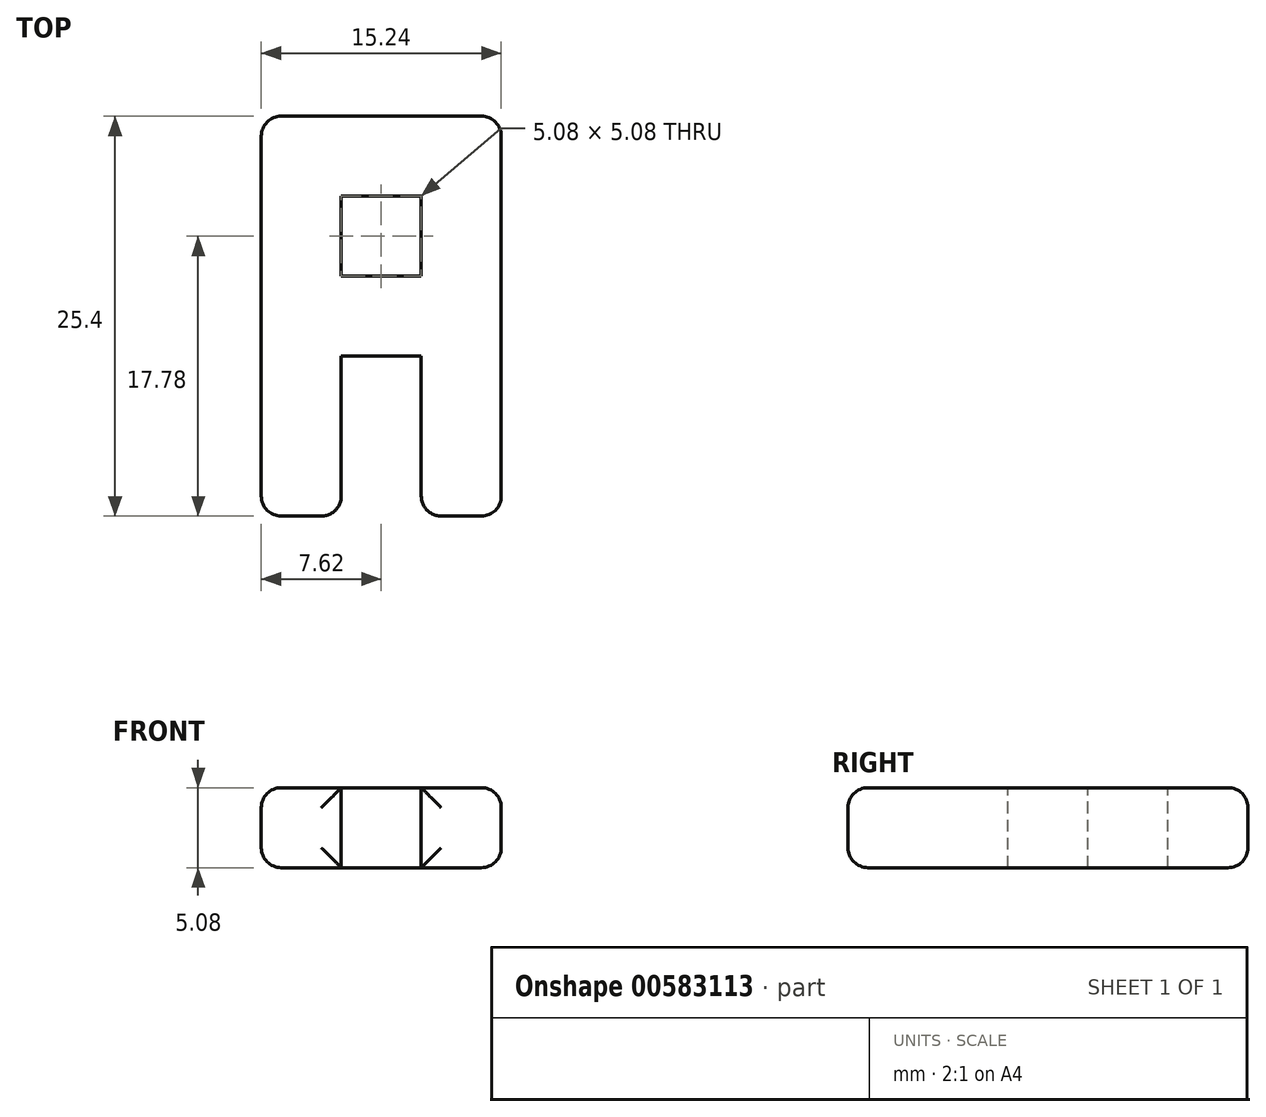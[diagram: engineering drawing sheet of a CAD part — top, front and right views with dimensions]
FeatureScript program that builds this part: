
annotation { "Feature Type Name" : "Feature", "Feature Type Description" : "" }
export const myFeature = defineFeature(function(context is Context, id is Id, definition is map)
    precondition{}
    {
        {
            var Q0;
            Q0=qCreatedBy(makeId("Top.planeOp"),FACE);
            var sketch = newSketch(context, id + "F0", { "sketchPlane" : qUnion([Q0])});
            skLineSegment(sketch, "E0.bottom", {"start": v(7.62, 12.7) * mm, "end": v(-7.62, 12.7) * mm});
            skLineSegment(sketch, "E0.top", {"start": v(7.62, -12.7) * mm, "end": v(-7.62, -12.7) * mm});
            skLineSegment(sketch, "E0.left", {"start": v(7.62, 12.7) * mm, "end": v(7.62, -12.7) * mm});
            skLineSegment(sketch, "E0.right", {"start": v(-7.62, 12.7) * mm, "end": v(-7.62, -12.7) * mm});
            skPoint(sketch, "E0.middle", {"position": v(0, 0) * mm});
            skSolve(sketch);
        }
        {
            var Q0;
            Q0=makeQuery(id+"F0.imprint","IMPRINT",FACE,{"disambiguationData":[TD([[makeQuery(id+"F0.imprint","IMPRINT",EDGE,{"derivedFrom":sQuery(id+"F0.wireOp",EDGE,"E0.bottom")}),1.0]])]});
            extrude(context, id + "F1", {"entities" : qUnion([Q0]), "depth" : 5.08 * mm, "offsetDistance" : 25.4 * mm});
        }
        {
            var Q0;
            Q0=makeQuery(id+"F1.opExtrude","CAP_FACE",FACE,{"disambiguationData":[OSD([sQuery(id+"F0.wireOp",EDGE,"E0.bottom"),sQuery(id+"F0.wireOp",EDGE,"E0.top"),sQuery(id+"F0.wireOp",EDGE,"E0.left"),sQuery(id+"F0.wireOp",EDGE,"E0.right")])],"isStart":false});
            var sketch = newSketch(context, id + "F2", { "sketchPlane" : qUnion([Q0])});
            skLineSegment(sketch, "E1.bottom", {"start": v(-2.54, -12.7) * mm, "end": v(2.54, -12.7) * mm});
            skLineSegment(sketch, "E1.top", {"start": v(-2.54, -2.54) * mm, "end": v(2.54, -2.54) * mm});
            skLineSegment(sketch, "E1.left", {"start": v(-2.54, -12.7) * mm, "end": v(-2.54, -2.54) * mm});
            skLineSegment(sketch, "E1.right", {"start": v(2.54, -12.7) * mm, "end": v(2.54, -2.54) * mm});
            skLineSegment(sketch, "E2.bottom", {"start": v(-2.54, 7.62) * mm, "end": v(2.54, 7.62) * mm});
            skLineSegment(sketch, "E2.top", {"start": v(-2.54, 2.54) * mm, "end": v(2.54, 2.54) * mm});
            skLineSegment(sketch, "E2.left", {"start": v(-2.54, 7.62) * mm, "end": v(-2.54, 2.54) * mm});
            skLineSegment(sketch, "E2.right", {"start": v(2.54, 7.62) * mm, "end": v(2.54, 2.54) * mm});
            skSolve(sketch);
        }
        {
            var Q0;
            Q0=makeQuery(id+"F2.imprint","IMPRINT",FACE,{"disambiguationData":[TD([[makeQuery(id+"F2.imprint","IMPRINT",EDGE,{"derivedFrom":sQuery(id+"F2.wireOp",EDGE,"E2.bottom")}),-1.0]])]});
            var Q1;
            Q1=makeQuery(id+"F2.imprint","IMPRINT",FACE,{"disambiguationData":[TD([[makeQuery(id+"F2.imprint","IMPRINT",EDGE,{"derivedFrom":sQuery(id+"F2.wireOp",EDGE,"E1.bottom")}),-1.0]])]});
            extrude(context, id + "F3", {"entities" : qUnion([Q0, Q1]), "operationType" : NewBodyOperationType.REMOVE, "oppositeDirection" : true, "depth" : 5.08 * mm, "offsetDistance" : 25.4 * mm});
        }
        {
            var Q0;
            Q0=makeQuery(id+"F1.opExtrude","SWEPT_EDGE",EDGE,{"disambiguationData":[OSD([sQuery(id+"F0.wireOp",EDGE,"E0.bottom"),sQuery(id+"F0.wireOp",EDGE,"E0.right")])]});
            var Q1;
            Q1=makeQuery(id+"F1.opExtrude","SWEPT_EDGE",EDGE,{"disambiguationData":[OSD([sQuery(id+"F0.wireOp",EDGE,"E0.top"),sQuery(id+"F0.wireOp",EDGE,"E0.right")])]});
            var Q2;
            Q2=makeQuery(id+"F3.boolean.opBoolean","COPY",EDGE,{"derivedFrom":makeQuery(id+"F3.opExtrude","CAP_EDGE",EDGE,{"disambiguationData":[OSD([sQuery(id+"F2.wireOp",EDGE,"E2.top")])],"isStart":true})});
            var Q3;
            Q3=makeQuery(id+"F3.boolean.opBoolean","COPY",EDGE,{"derivedFrom":makeQuery(id+"F3.opExtrude","CAP_EDGE",EDGE,{"disambiguationData":[OSD([sQuery(id+"F2.wireOp",EDGE,"E2.right")])],"isStart":true})});
            var Q4;
            Q4=makeQuery(id+"F3.boolean.opBoolean","COPY",EDGE,{"derivedFrom":makeQuery(id+"F3.opExtrude","CAP_EDGE",EDGE,{"disambiguationData":[OSD([sQuery(id+"F2.wireOp",EDGE,"E2.left")])],"isStart":true})});
            var Q5;
            Q5=makeQuery(id+"F3.boolean.opBoolean","COPY",EDGE,{"derivedFrom":makeQuery(id+"F3.opExtrude","CAP_EDGE",EDGE,{"disambiguationData":[OSD([sQuery(id+"F2.wireOp",EDGE,"E2.bottom")])],"isStart":true})});
            var Q6;
            Q6=makeQuery(id+"F1.opExtrude","CAP_EDGE",EDGE,{"disambiguationData":[OSD([sQuery(id+"F0.wireOp",EDGE,"E0.bottom")])],"isStart":false});
            var Q7;
            Q7=makeQuery(id+"F1.opExtrude","CAP_EDGE",EDGE,{"disambiguationData":[OSD([sQuery(id+"F0.wireOp",EDGE,"E0.bottom")])],"isStart":true});
            var Q8;
            Q8=makeQuery(id+"F1.opExtrude","SWEPT_EDGE",EDGE,{"disambiguationData":[OSD([sQuery(id+"F0.wireOp",EDGE,"E0.bottom"),sQuery(id+"F0.wireOp",EDGE,"E0.left")])]});
            var Q9;
            Q9=makeQuery(id+"F3.boolean.opBoolean","COPY",EDGE,{"derivedFrom":makeQuery(id+"F3.opExtrude","CAP_EDGE",EDGE,{"disambiguationData":[OSD([sQuery(id+"F2.wireOp",EDGE,"E1.top")])],"isStart":true})});
            var Q10;
            Q10=makeQuery(id+"F3.boolean.opBoolean","COPY",EDGE,{"derivedFrom":makeQuery(id+"F3.opExtrude","CAP_EDGE",EDGE,{"disambiguationData":[OSD([sQuery(id+"F2.wireOp",EDGE,"E1.top")])],"isStart":false})});
            var Q11;
            Q11=makeQuery(id+"F3.boolean.opBoolean","COPY",EDGE,{"derivedFrom":makeQuery(id+"F3.opExtrude","CAP_EDGE",EDGE,{"disambiguationData":[OSD([sQuery(id+"F2.wireOp",EDGE,"E1.right")])],"isStart":true})});
            var Q12;
            Q12=makeQuery(id+"F3.boolean.opBoolean","COPY",EDGE,{"derivedFrom":makeQuery(id+"F3.opExtrude","CAP_EDGE",EDGE,{"disambiguationData":[OSD([sQuery(id+"F2.wireOp",EDGE,"E1.left")])],"isStart":true})});
            var Q13;
            Q13=makeQuery(id+"F1.opExtrude","CAP_EDGE",EDGE,{"disambiguationData":[OSD([sQuery(id+"F0.wireOp",EDGE,"E0.left")])],"isStart":true});
            var Q14;
            Q14=makeQuery(id+"F1.opExtrude","CAP_EDGE",EDGE,{"disambiguationData":[OSD([sQuery(id+"F0.wireOp",EDGE,"E0.left")])],"isStart":false});
            var Q15;
            Q15=makeQuery(id+"F1.opExtrude","SWEPT_EDGE",EDGE,{"disambiguationData":[OSD([sQuery(id+"F0.wireOp",EDGE,"E0.top"),sQuery(id+"F0.wireOp",EDGE,"E0.left")])]});
            var Q16;
            {var subQ0=sQuery(id+"F0.wireOp",EDGE,"E0.left");var subQ1=sQuery(id+"F0.wireOp",EDGE,"E0.top");Q16=makeQuery(id+"F3.boolean.opBoolean","SPLIT",EDGE,{"disambiguationData":[TD([makeQuery(id+"F1.opExtrude","SWEPT_FACE",FACE,{"disambiguationData":[OSD([subQ0])]})])],"derivedFrom":makeQuery(id+"F1.opExtrude","CAP_EDGE",EDGE,{"disambiguationData":[OSD([subQ1])],"isStart":false})});}
            var Q17;
            {var subQ1=sQuery(id+"F0.wireOp",EDGE,"E0.left");var subQ2=sQuery(id+"F0.wireOp",EDGE,"E0.top");Q17=makeQuery(id+"F3.boolean.opBoolean","SPLIT",FACE,{"disambiguationData":[TD([makeQuery(id+"F1.opExtrude","SWEPT_FACE",FACE,{"disambiguationData":[OSD([subQ1])]})])],"derivedFrom":makeQuery(id+"F1.opExtrude","SWEPT_FACE",FACE,{"disambiguationData":[OSD([subQ2])]})});}
            var Q18;
            {var subQ0=sQuery(id+"F0.wireOp",EDGE,"E0.right");var subQ1=sQuery(id+"F0.wireOp",EDGE,"E0.top");Q18=makeQuery(id+"F3.boolean.opBoolean","SPLIT",EDGE,{"disambiguationData":[TD([makeQuery(id+"F1.opExtrude","SWEPT_FACE",FACE,{"disambiguationData":[OSD([subQ0])]})])],"derivedFrom":makeQuery(id+"F1.opExtrude","CAP_EDGE",EDGE,{"disambiguationData":[OSD([subQ1])],"isStart":false})});}
            var Q19;
            Q19=makeQuery(id+"F3.boolean.opBoolean","COPY",EDGE,{"derivedFrom":makeQuery(id+"F3.opExtrude","SWEPT_EDGE",EDGE,{"disambiguationData":[OSD([sQuery(id+"F0.wireOp",EDGE,"E0.top"),sQuery(id+"F2.wireOp",EDGE,"E1.bottom"),sQuery(id+"F2.wireOp",EDGE,"E1.left")])]})});
            var Q20;
            Q20=makeQuery(id+"F1.opExtrude","CAP_EDGE",EDGE,{"disambiguationData":[OSD([sQuery(id+"F0.wireOp",EDGE,"E0.right")])],"isStart":false});
            var Q21;
            {var subQ0=sQuery(id+"F0.wireOp",EDGE,"E0.right");var subQ1=sQuery(id+"F0.wireOp",EDGE,"E0.top");Q21=makeQuery(id+"F3.boolean.opBoolean","SPLIT",EDGE,{"disambiguationData":[TD([makeQuery(id+"F1.opExtrude","SWEPT_FACE",FACE,{"disambiguationData":[OSD([subQ0])]})])],"derivedFrom":makeQuery(id+"F1.opExtrude","CAP_EDGE",EDGE,{"disambiguationData":[OSD([subQ1])],"isStart":true})});}
            var Q22;
            Q22=makeQuery(id+"F3.boolean.opBoolean","COPY",EDGE,{"derivedFrom":makeQuery(id+"F3.opExtrude","CAP_EDGE",EDGE,{"disambiguationData":[OSD([sQuery(id+"F2.wireOp",EDGE,"E2.top")])],"isStart":false})});
            var Q23;
            Q23=makeQuery(id+"F3.boolean.opBoolean","COPY",EDGE,{"derivedFrom":makeQuery(id+"F3.opExtrude","CAP_EDGE",EDGE,{"disambiguationData":[OSD([sQuery(id+"F2.wireOp",EDGE,"E2.left")])],"isStart":false})});
            var Q24;
            Q24=makeQuery(id+"F3.boolean.opBoolean","COPY",EDGE,{"derivedFrom":makeQuery(id+"F3.opExtrude","CAP_EDGE",EDGE,{"disambiguationData":[OSD([sQuery(id+"F2.wireOp",EDGE,"E2.bottom")])],"isStart":false})});
            var Q25;
            Q25=makeQuery(id+"F3.boolean.opBoolean","COPY",EDGE,{"derivedFrom":makeQuery(id+"F3.opExtrude","CAP_EDGE",EDGE,{"disambiguationData":[OSD([sQuery(id+"F2.wireOp",EDGE,"E2.right")])],"isStart":false})});
            var Q26;
            Q26=makeQuery(id+"F1.opExtrude","CAP_EDGE",EDGE,{"disambiguationData":[OSD([sQuery(id+"F0.wireOp",EDGE,"E0.right")])],"isStart":true});
            var Q27;
            Q27=makeQuery(id+"F3.boolean.opBoolean","COPY",EDGE,{"derivedFrom":makeQuery(id+"F3.opExtrude","CAP_EDGE",EDGE,{"disambiguationData":[OSD([sQuery(id+"F2.wireOp",EDGE,"E1.left")])],"isStart":false})});
            var Q28;
            Q28=makeQuery(id+"F3.boolean.opBoolean","COPY",EDGE,{"derivedFrom":makeQuery(id+"F3.opExtrude","CAP_EDGE",EDGE,{"disambiguationData":[OSD([sQuery(id+"F2.wireOp",EDGE,"E1.right")])],"isStart":false})});
            fillet(context, id + "F4", {"entities" : qUnion([Q0, Q1, Q2, Q3, Q4, Q5, Q6, Q7, Q8, Q9, Q10, Q11, Q12, Q13, Q14, Q15, Q16, Q17, Q18, Q19, Q20, Q21, Q22, Q23, Q24, Q25, Q26, Q27, Q28]), "radius" : 1.27 * mm, "tangentPropagation" : true, "allowEdgeOverflow" : false});
        }
    });
